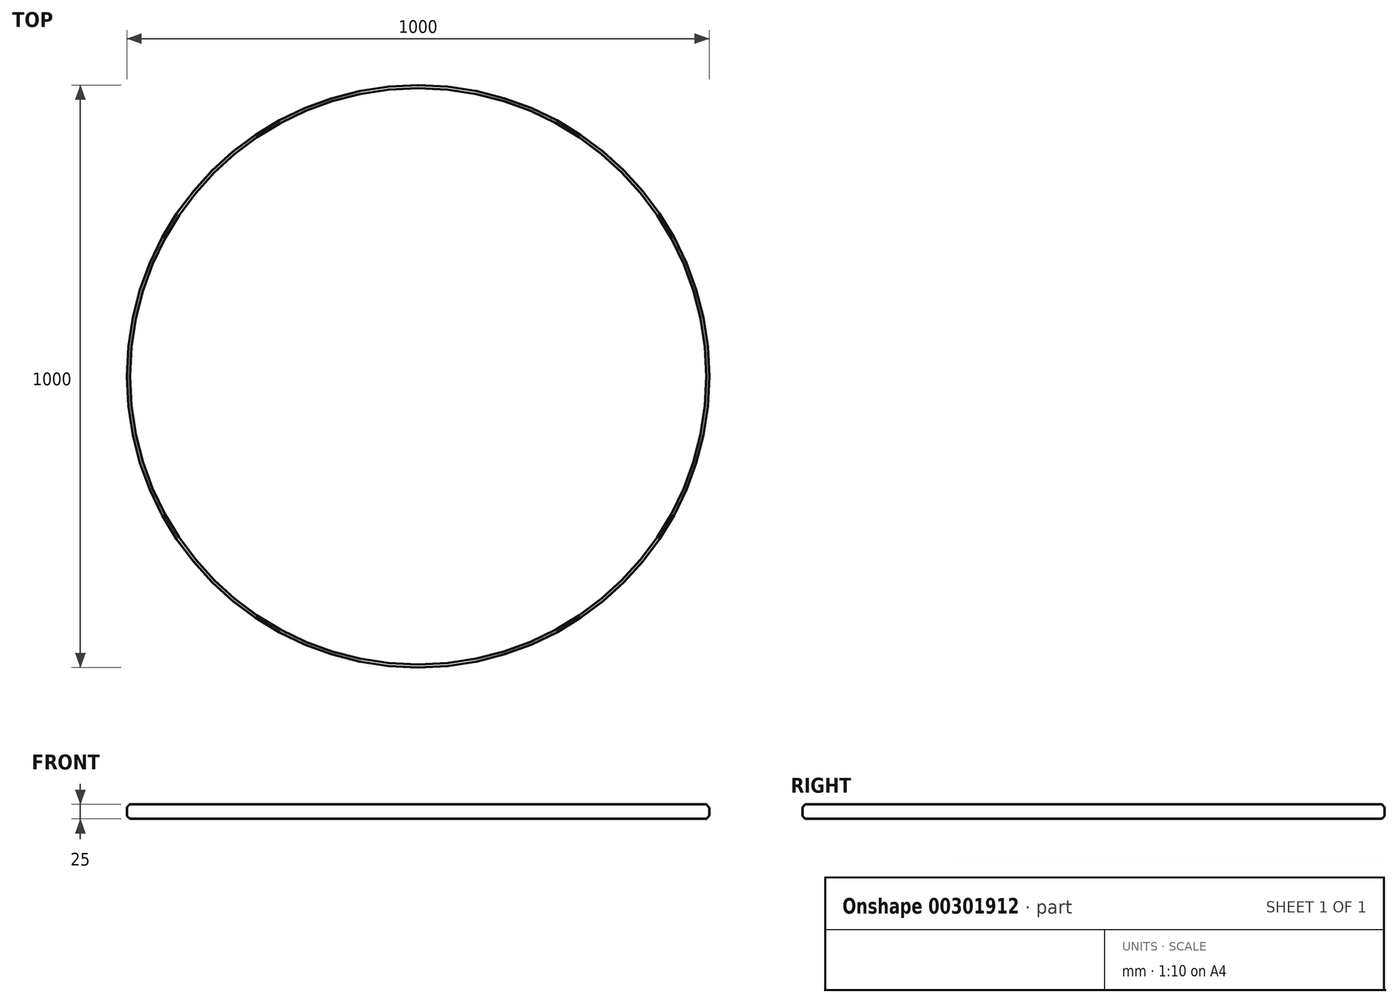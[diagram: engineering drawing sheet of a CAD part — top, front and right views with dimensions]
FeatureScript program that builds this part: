
annotation { "Feature Type Name" : "Feature", "Feature Type Description" : "" }
export const myFeature = defineFeature(function(context is Context, id is Id, definition is map)
    precondition{}
    {
        {
            var Q0;
            Q0=qCreatedBy(makeId("Top.planeOp"),FACE);
            var sketch = newSketch(context, id + "F0", { "sketchPlane" : qUnion([Q0])});
            skCircle(sketch, "E0", {"center": v(0, 0) * mm, "radius": 500 * mm});
            skSolve(sketch);
        }
        {
            var Q0;
            Q0=makeQuery(id+"F0.imprint","IMPRINT",FACE,{"disambiguationData":[TD([[makeQuery(id+"F0.imprint","IMPRINT",EDGE,{"derivedFrom":sQuery(id+"F0.wireOp",EDGE,"E0")}),1.0]])]});
            extrude(context, id + "F1", {"entities" : qUnion([Q0]), "depth" : 25 * mm});
        }
        {
            var Q0;
            Q0=makeQuery(id+"F1.opExtrude","CAP_EDGE",EDGE,{"disambiguationData":[OSD([sQuery(id+"F0.wireOp",EDGE,"E0")])],"isStart":false});
            var Q1;
            Q1=makeQuery(id+"F1.opExtrude","CAP_EDGE",EDGE,{"disambiguationData":[OSD([sQuery(id+"F0.wireOp",EDGE,"E0")])],"isStart":true});
            chamfer(context, id + "F2", {"entities" : qUnion([Q0, Q1]), "width" : 5 * mm, "tangentPropagation" : true});
        }
        {
            var Q0;
            Q0=makeQuery(id+"F1.opExtrude","SWEPT_FACE",FACE,{"disambiguationData":[OSD([sQuery(id+"F0.wireOp",EDGE,"E0")])]});
            fillet(context, id + "F3", {"entities" : qUnion([Q0]), "radius" : 5 * mm, "tangentPropagation" : true, "allowEdgeOverflow" : false});
        }
    });
